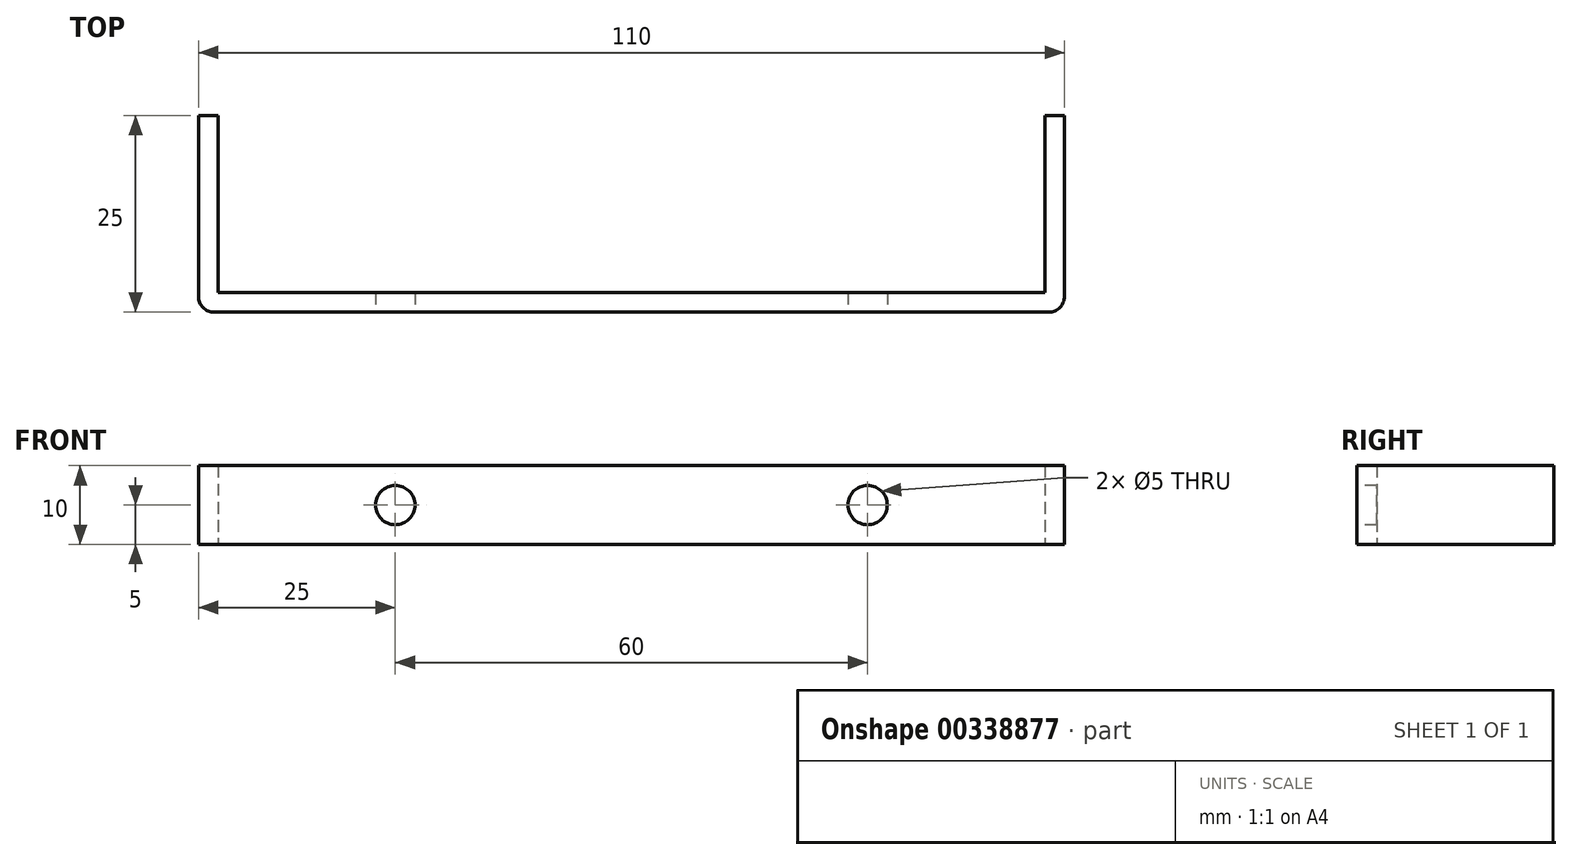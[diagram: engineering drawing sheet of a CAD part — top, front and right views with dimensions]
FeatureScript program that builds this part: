
annotation { "Feature Type Name" : "Feature", "Feature Type Description" : "" }
export const myFeature = defineFeature(function(context is Context, id is Id, definition is map)
    precondition{}
    {
        {
            var Q0;
            Q0=qCreatedBy(makeId("Front.planeOp"),FACE);
            var sketch = newSketch(context, id + "F0", { "sketchPlane" : qUnion([Q0])});
            skLineSegment(sketch, "E0.bottom", {"start": v(-55, 5) * mm, "end": v(55, 5) * mm});
            skLineSegment(sketch, "E0.top", {"start": v(-55, -5) * mm, "end": v(55, -5) * mm});
            skLineSegment(sketch, "E0.left", {"start": v(-55, 5) * mm, "end": v(-55, -5) * mm});
            skLineSegment(sketch, "E0.right", {"start": v(55, 5) * mm, "end": v(55, -5) * mm});
            skPoint(sketch, "E0.middle", {"position": v(0, 0) * mm});
            skCircle(sketch, "E1", {"center": v(-30, 0) * mm, "radius": 2.5 * mm});
            skCircle(sketch, "E2", {"center": v(30, 0) * mm, "radius": 2.5 * mm});
            skSolve(sketch);
        }
        {
            var Q0;
            Q0 = qSketchRegion(id + "F0", true);
            extrude(context, id + "F1", {"entities" : qUnion([Q0]), "flatOperationType" : FlatOperationType.REMOVE, "oppositeDirection" : true, "offsetDistance" : 25 * mm, "depth" : 25 * mm, "domain" : OperationDomain.MODEL});
        }
        {
            var Q0;
            Q0=makeQuery(id+"F1.opExtrude","SWEPT_FACE",FACE,{"disambiguationData":[OSD([sQuery(id+"F0.wireOp",EDGE,"E0.top")])]});
            var Q1;
            Q1=makeQuery(id+"F1.opExtrude","CAP_FACE",FACE,{"disambiguationData":[OSD([sQuery(id+"F0.wireOp",EDGE,"E0.bottom"),sQuery(id+"F0.wireOp",EDGE,"E0.top"),sQuery(id+"F0.wireOp",EDGE,"E0.left"),sQuery(id+"F0.wireOp",EDGE,"E0.right"),sQuery(id+"F0.wireOp",EDGE,"G7nlwj17-Flki-QOPu-pENh-9XlGJTdqkPnG")])],"isStart":false});
            var Q2;
            Q2=makeQuery(id+"F1.opExtrude","SWEPT_FACE",FACE,{"disambiguationData":[OSD([sQuery(id+"F0.wireOp",EDGE,"E0.bottom")])]});
            var Q3;
            Q3=makeQuery(id+"F1.opExtrude","SWEPT_FACE",FACE,{"disambiguationData":[OSD([sQuery(id+"F0.wireOp",EDGE,"G7nlwj17-Flki-QOPu-pENh-9XlGJTdqkPnG")])]});
            var Q4;
            Q4=makeQuery(id+"F1.opExtrude","SWEPT_FACE",FACE,{"disambiguationData":[OSD([sQuery(id+"F0.wireOp",EDGE,"E1")])]});
            var Q5;
            Q5=makeQuery(id+"F1.opExtrude","SWEPT_FACE",FACE,{"disambiguationData":[OSD([sQuery(id+"F0.wireOp",EDGE,"E2")])]});
            shell(context, id + "F2", {"entities" : qUnion([Q0, Q1, Q2, Q3, Q4, Q5]), "thickness" : 2.5 * mm});
        }
        {
            var Q0;
            Q0=makeQuery(id+"F1.opExtrude","CAP_EDGE",EDGE,{"disambiguationData":[OSD([sQuery(id+"F0.wireOp",EDGE,"E0.left")])],"isStart":true});
            var Q1;
            Q1=makeQuery(id+"F1.opExtrude","CAP_EDGE",EDGE,{"disambiguationData":[OSD([sQuery(id+"F0.wireOp",EDGE,"E0.right")])],"isStart":true});
            fillet(context, id + "F3", {"entities" : qUnion([Q0, Q1]), "radius" : 2 * mm, "tangentPropagation" : true, "defaultsChanged" : false, "allowEdgeOverflow" : false, "vertexSettings" : [], "filletType" : FilletType.EDGE});
        }
    });
